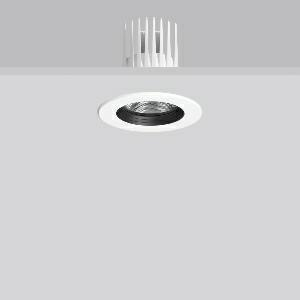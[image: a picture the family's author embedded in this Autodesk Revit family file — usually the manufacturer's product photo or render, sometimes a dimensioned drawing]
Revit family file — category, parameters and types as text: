
# Revit family: heledon_mini_e_901742_002_3_76_f661
name_source: partatom
category: Lighting Fixtures
units: mm (PartAtom-declared; Revit-internal decimal feet)

## family parameters
Cut with Voids When Loaded = No
Host = Face
Light Source = No
Part Type = Normal
Room Calculation Point = No
Round Connector Dimension = Use Diameter
Shared = No

## types (1)
- HELEDON mini E (1 x LED Modul 935, 2650 lm, 3500)
    Apparent Load = 20 VA
    Approval mark = CE
    CIE Flux Codes = 95 99 100 100 100
    Color Rendering = 92
    Color Temperature = 3500
    Default Elevation = 1800 mm
    Description = Series: HELEDON mini
Round recessed downlight. Housing: die-cast aluminium, powder-coated. Black plastic ring and recessed LED to prevent glare from the side. Optical assembly with reflector made of MIRO-Silver with 98% total light reflection for outstanding efficiency - can be changed without tools. Best colour rendering index Ra>90. Suitable for Recessed ceiling mounting. Installation without tools thanks to spring fastening system. Including separate LED converter with connecting cable 600 mm.High quality converter without flickering and stroboscopic effect. Through-wiring box (5 pole) available as accessory. The following accessories can be mounted without use of tools: interchangeable lenses, decorative glasses, honeycomb louvre, clear and frosted diffusers, white interchangeable plastic ring. 
Colour: traffic white, matt (RAL 9016)
Diameter: 124 mm
Height: 3 mm
Cut-out diameter: 114 mm
Recess height: 170 mm
Luminaire: recess height: 120 mm
Lamp: LED
Socket: without socket
Colour temperature: 3500K
Colour rendering index (CRI): 92
System power: 20 W
Rated luminous flux: 2650 lm
Luminous efficiency: 133 lm/W
Control gear: Converter, dimmable, DALI
Protection class: II
Type of protection: IP 20
    Height = 0 mm  [stored 0 ft]
    Lamp = 1 x LED Modul 935
    Lamp Light Flux = 2650 lm
    Lamp count = 1
    Length = 124 mm  [stored 0.406824 ft]
    Lifetime = 50000 h
    Luminous efficacy = 133 lm/W
    Manufacturer = RZB
    ModVariant = No
    Model = 901742.002.3.76
    Mounting Place = Ceiling
    Mounting Type = Recessed
    Number of Poles = 1
    OnlyDefault = Yes
    Power Factor = 1
    Product Name = HELEDON mini E
    Product group = Recessed downlights
    ProductGroupID = 402
    Protection Class = Protection class II
    Protection Degree = IP 20
    RLX_Detail_Level = 1
    RLX_Emergency_Light_Flux = 0 lm
    RLX_Emergency_Type = 0
    RLX_Emergency_Type_DB = No
    RlxData = <blob elided: 126893 chars, md5=eb0814ff>
    Socket = socket
    Standby Power = 0 W
    System Light Flux = 2650 lm
    System Power = 20 W
    Type Comments = Product without accessories
    Type Image = 901657.002.jpg
    URL = http://relux.com
    VarID = ---
    Voltage = 230 V
    Voltage Range = 220-240 V
    Weight = 0.00 kg
    Width = 0 mm  [stored 0 ft]

note: [stored X ft] marks values corroborated as IEEE doubles in the binary element streams (Revit-internal decimal feet)

## geometry (parser evidence)
native form markers: Blend x4, Sweep x11
no freeform markers — native parametric forms only
